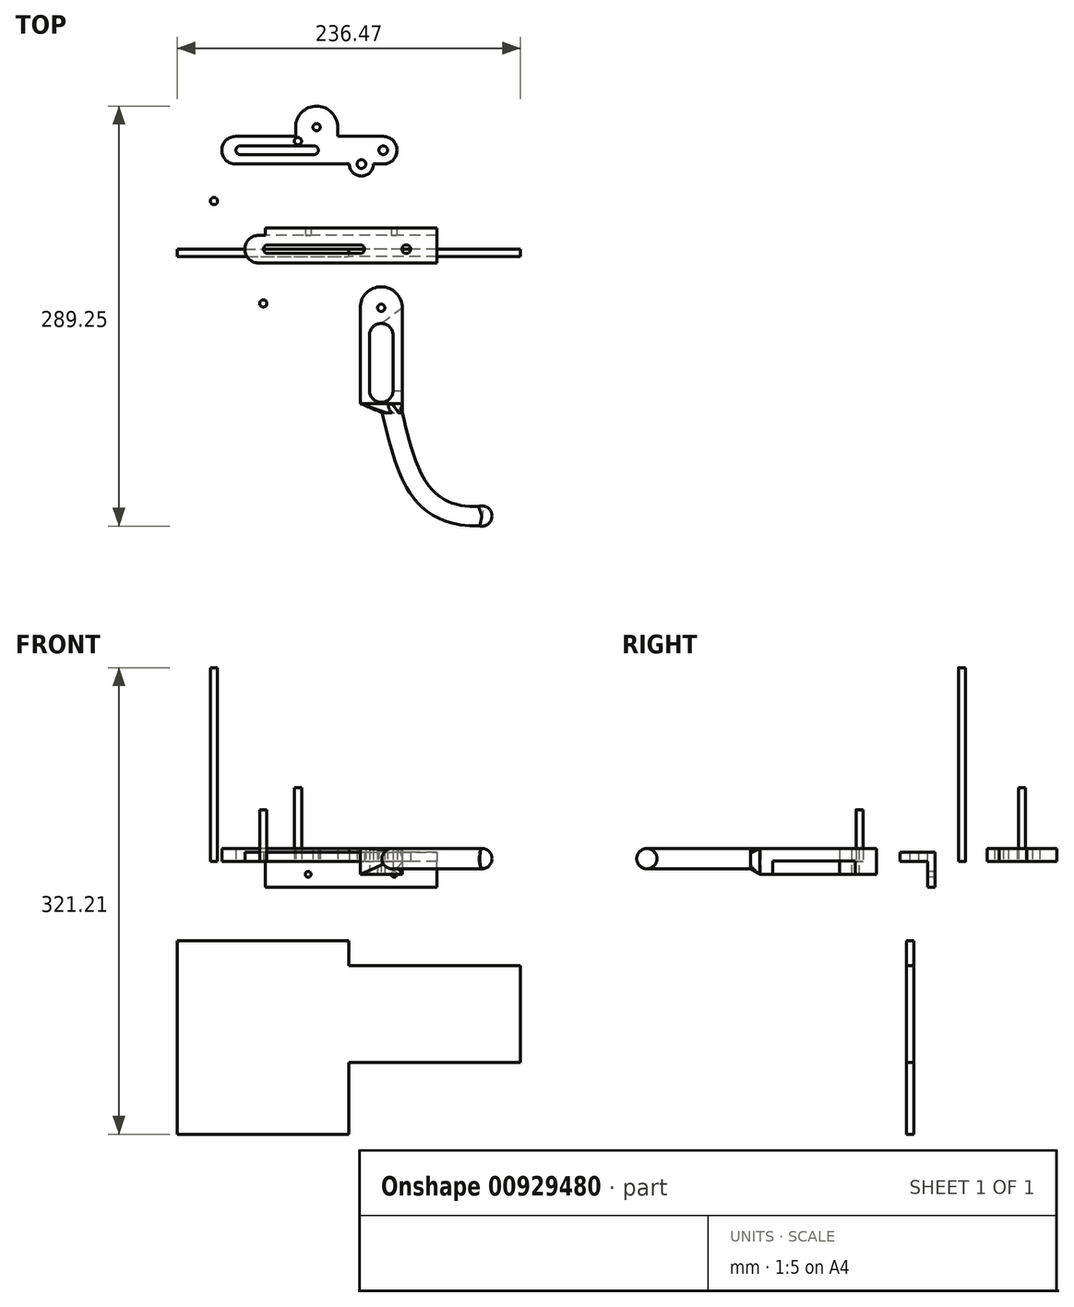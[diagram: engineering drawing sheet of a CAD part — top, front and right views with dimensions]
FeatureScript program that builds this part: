
annotation { "Feature Type Name" : "Feature", "Feature Type Description" : "" }
export const myFeature = defineFeature(function(context is Context, id is Id, definition is map)
    precondition{}
    {
        {
            var Q0;
            Q0=qCreatedBy(makeId("Top.planeOp"),FACE);
            var sketch = newSketch(context, id + "F0", { "sketchPlane" : qUnion([Q0])});
            skLineSegment(sketch, "E0.bottom", {"start": v(63.5, 9.53) * mm, "end": v(-38.1, 9.52) * mm});
            skLineSegment(sketch, "E0.top", {"start": v(63.5, -9.52) * mm, "end": v(-38.1, -9.53) * mm});
            skPoint(sketch, "E0.middle", {"position": v(0, 0) * mm});
            skLineSegment(sketch, "E1.bottom", {"start": v(31.75, 3) * mm, "end": v(-31.75, 3) * mm});
            skLineSegment(sketch, "E1.top", {"start": v(31.75, -3) * mm, "end": v(-31.75, -3) * mm});
            skArc(sketch, "E2", {"start": v(-31.75, 3) * mm, "mid": v(-34.75, 0) * mm, "end": v(-31.75, -3) * mm});
            skArc(sketch, "E3", {"start": v(31.75, -3) * mm, "mid": v(34.75, 0) * mm, "end": v(31.75, 3) * mm});
            skArc(sketch, "E4", {"start": v(-38.1, 9.52) * mm, "mid": v(-47.62, 0) * mm, "end": v(-38.1, -9.53) * mm});
            skLineSegment(sketch, "E5.bottom", {"start": v(63.5, 9.53) * mm, "end": v(84.7, 9.53) * mm});
            skLineSegment(sketch, "E5.top", {"start": v(63.5, -9.52) * mm, "end": v(84.7, -9.52) * mm});
            skLineSegment(sketch, "E5.right", {"start": v(84.7, 9.53) * mm, "end": v(84.7, -9.52) * mm});
            skCircle(sketch, "E6", {"center": v(63.5, 0) * mm, "radius": 3 * mm});
            skSolve(sketch);
        }
        {
            var Q0;
            Q0=makeQuery(id+"F0.imprint","IMPRINT",FACE,{"disambiguationData":[TD([[makeQuery(id+"F0.imprint","IMPRINT",EDGE,{"derivedFrom":sQuery(id+"F0.wireOp",EDGE,"E0.bottom")}),1.0]])]});
            extrude(context, id + "F1", {"entities" : qUnion([Q0]), "depth" : 6.35 * mm, "offsetDistance" : 25.4 * mm});
        }
        {
            var Q0;
            Q0=qCreatedBy(makeId("Top.planeOp"),FACE);
            var sketch = newSketch(context, id + "F2", { "sketchPlane" : qUnion([Q0])});
            skLineSegment(sketch, "E7.bottom", {"start": v(47.62, 77.65) * mm, "end": v(16.26, 77.65) * mm});
            skLineSegment(sketch, "E7.top", {"start": v(47.62, 58.6) * mm, "end": v(-53.98, 58.6) * mm});
            skLineSegment(sketch, "E8.bottom", {"start": v(0, 71.13) * mm, "end": v(-50.8, 71.13) * mm});
            skLineSegment(sketch, "E8.top", {"start": v(0, 65.13) * mm, "end": v(-50.8, 65.13) * mm});
            skPoint(sketch, "E8.middle", {"position": v(-25.4, 68.13) * mm});
            skArc(sketch, "E9", {"start": v(-50.8, 71.13) * mm, "mid": v(-53.8, 68.13) * mm, "end": v(-50.8, 65.13) * mm});
            skArc(sketch, "E10", {"start": v(0, 65.13) * mm, "mid": v(3, 68.13) * mm, "end": v(0, 71.13) * mm});
            skArc(sketch, "E11", {"start": v(-53.98, 77.65) * mm, "mid": v(-63.5, 68.13) * mm, "end": v(-53.98, 58.6) * mm});
            skArc(sketch, "E12", {"start": v(47.62, 58.6) * mm, "mid": v(57.15, 68.13) * mm, "end": v(47.62, 77.65) * mm});
            skLineSegment(sketch, "E13", {"start": v(-25.4, 77.65) * mm, "end": v(-25.4, 58.6) * mm, "construction": true});
            skCircle(sketch, "E14", {"center": v(47.62, 68.13) * mm, "radius": 3 * mm});
            skCircle(sketch, "E15", {"center": v(32.61, 58.6) * mm, "radius": 3 * mm});
            skArc(sketch, "E16", {"start": v(24.32, 58.6) * mm, "mid": v(32.61, 50.31) * mm, "end": v(40.9, 58.6) * mm});
            skArc(sketch, "E17", {"start": v(16.26, 84) * mm, "mid": v(1.78, 98.48) * mm, "end": v(-12.7, 84) * mm});
            skCircle(sketch, "E18", {"center": v(1.78, 84) * mm, "radius": 2.5 * mm});
            skLineSegment(sketch, "E19", {"start": v(-12.7, 77.65) * mm, "end": v(-12.7, 84) * mm});
            skLineSegment(sketch, "E20", {"start": v(16.26, 77.65) * mm, "end": v(16.26, 84) * mm});
            skLineSegment(sketch, "E21", {"start": v(-12.7, 77.65) * mm, "end": v(-53.98, 77.65) * mm});
            skSolve(sketch);
        }
        {
            var Q0;
            Q0=makeQuery(id+"F2.imprint","IMPRINT",FACE,{"disambiguationData":[TD([[makeQuery(id+"F2.imprint","IMPRINT",EDGE,{"derivedFrom":sQuery(id+"F2.wireOp",EDGE,"E7.bottom")}),1.0]])]});
            var Q1;
            {var subQ0=sQuery(id+"F2.wireOp",EDGE,"O4J8zJx1-k10I-jmTt-IUS2-t3sebLQ1dyLB");Q1=makeQuery(id+"F2.imprint","IMPRINT",FACE,{"disambiguationData":[TD([[makeQuery(id+"F2.imprint","IMPRINT",EDGE,{"derivedFrom":subQ0}),1.0]])]});}
            var Q2;
            {var subQ0=sQuery(id+"F2.wireOp",EDGE,"E16");Q2=makeQuery(id+"F2.imprint","IMPRINT",FACE,{"disambiguationData":[TD([[makeQuery(id+"F2.imprint","IMPRINT",EDGE,{"derivedFrom":subQ0}),1.0]])]});}
            extrude(context, id + "F3", {"entities" : qUnion([Q0, Q1, Q2]), "depth" : 9 * mm, "offsetDistance" : 25.4 * mm});
        }
        {
            var Q0;
            Q0=qCreatedBy(makeId("Top.planeOp"),FACE);
            var sketch = newSketch(context, id + "F4", { "sketchPlane" : qUnion([Q0])});
            skCircle(sketch, "E22", {"center": v(-11.08, 74.38) * mm, "radius": 2.5 * mm});
            skSolve(sketch);
        }
        {
            var Q0;
            Q0=makeQuery(id+"F4.imprint","IMPRINT",FACE,{"disambiguationData":[TD([[makeQuery(id+"F4.imprint","IMPRINT",EDGE,{"derivedFrom":sQuery(id+"F4.wireOp",EDGE,"E22")}),1.0]])]});
            extrude(context, id + "F5", {"entities" : qUnion([Q0]), "depth" : 50.8 * mm, "offsetDistance" : 25.4 * mm});
        }
        {
            var Q0;
            Q0=qCreatedBy(makeId("Top.planeOp"),FACE);
            var sketch = newSketch(context, id + "F6", { "sketchPlane" : qUnion([Q0])});
            skCircle(sketch, "E23", {"center": v(-34.92, -37.39) * mm, "radius": 2.5 * mm});
            skSolve(sketch);
        }
        {
            var Q0;
            Q0=makeQuery(id+"F6.imprint","IMPRINT",FACE,{"disambiguationData":[TD([[makeQuery(id+"F6.imprint","IMPRINT",EDGE,{"derivedFrom":sQuery(id+"F6.wireOp",EDGE,"E23")}),1.0]])]});
            extrude(context, id + "F7", {"entities" : qUnion([Q0]), "depth" : 35.56 * mm, "offsetDistance" : 25.4 * mm});
        }
        {
            var Q0;
            Q0=qCreatedBy(makeId("Top.planeOp"),FACE);
            var sketch = newSketch(context, id + "F8", { "sketchPlane" : qUnion([Q0])});
            skArc(sketch, "E24", {"start": v(54.38, -59.26) * mm, "mid": v(46.25, -51.13) * mm, "end": v(38.12, -59.26) * mm});
            skLineSegment(sketch, "E25.left", {"start": v(38.12, -59.26) * mm, "end": v(38.12, -97.36) * mm});
            skLineSegment(sketch, "E25.right", {"start": v(54.38, -59.26) * mm, "end": v(54.38, -97.36) * mm});
            skArc(sketch, "E26", {"start": v(38.12, -97.36) * mm, "mid": v(46.25, -105.49) * mm, "end": v(54.38, -97.36) * mm});
            skLineSegment(sketch, "E27.0", {"start": v(31.77, -62.87) * mm, "end": v(31.77, -97.36) * mm});
            skLineSegment(sketch, "E27.2", {"start": v(60.73, -62.87) * mm, "end": v(60.73, -97.36) * mm});
            skLineSegment(sketch, "E28.left", {"start": v(60.73, -62.87) * mm, "end": v(60.73, -40.39) * mm});
            skLineSegment(sketch, "E28.right", {"start": v(31.77, -62.87) * mm, "end": v(31.77, -40.39) * mm});
            skArc(sketch, "E29", {"start": v(60.73, -40.39) * mm, "mid": v(46.25, -25.91) * mm, "end": v(31.77, -40.39) * mm});
            skCircle(sketch, "E30", {"center": v(46.25, -40.39) * mm, "radius": 2.5 * mm});
            skLineSegment(sketch, "E31", {"start": v(60.73, -97.36) * mm, "end": v(60.73, -106.25) * mm});
            skLineSegment(sketch, "E32", {"start": v(60.73, -106.25) * mm, "end": v(31.77, -106.25) * mm});
            skLineSegment(sketch, "E33", {"start": v(31.77, -106.25) * mm, "end": v(31.77, -97.36) * mm});
            skSolve(sketch);
        }
        {
            var Q0;
            Q0=makeQuery(id+"F8.imprint","IMPRINT",FACE,{"disambiguationData":[TD([[makeQuery(id+"F8.imprint","IMPRINT",EDGE,{"derivedFrom":sQuery(id+"F8.wireOp",EDGE,"E24")}),-1.0]])]});
            extrude(context, id + "F9", {"entities" : qUnion([Q0]), "depth" : 8.9 * mm, "offsetDistance" : 25.4 * mm, "hasSecondDirection" : true, "secondDirectionOppositeDirection" : true, "secondDirectionDepth" : 8.9 * mm});
        }
        {
            var Q0;
            Q0=makeQuery(id+"F9.opExtrude","SWEPT_FACE",FACE,{"disambiguationData":[OSD([sQuery(id+"F8.wireOp",EDGE,"E32")])]});
            var sketch = newSketch(context, id + "F10", { "sketchPlane" : qUnion([Q0])});
            skLineSegment(sketch, "E34.bottom", {"start": v(31.77, 8.9) * mm, "end": v(60.73, 8.9) * mm});
            skLineSegment(sketch, "E34.top", {"start": v(31.77, -8.9) * mm, "end": v(60.73, -8.9) * mm});
            skLineSegment(sketch, "E34.left", {"start": v(31.77, 8.9) * mm, "end": v(31.77, -8.9) * mm});
            skLineSegment(sketch, "E34.right", {"start": v(60.73, 8.9) * mm, "end": v(60.73, -8.9) * mm});
            skSolve(sketch);
        }
        {
            var Q0;
            Q0=makeQuery(id+"F10.imprint","IMPRINT",FACE,{"disambiguationData":[TD([[makeQuery(id+"F10.imprint","IMPRINT",EDGE,{"derivedFrom":sQuery(id+"F10.wireOp",EDGE,"E34.bottom")}),1.0]])]});
            cPlane(context, id + "F11", {"entities" : qUnion([Q0]), "cplaneType" : CPlaneType.OFFSET, "offset" : 6.35 * mm, "width" : 152.4 * mm, "height" : 152.4 * mm});
        }
        {
            var Q0;
            Q0=qCreatedBy(id+"F11.planeOp",FACE);
            var sketch = newSketch(context, id + "F12", { "sketchPlane" : qUnion([Q0])});
            skCircle(sketch, "E35", {"center": v(53.74, 1.9) * mm, "radius": 6.99 * mm});
            skSolve(sketch);
        }
        {
            var Q0;
            Q0 = qConstructionFilter(qBodyType(qCreatedBy(id + "F14" ,EDGE), BodyType.WIRE), ConstructionObject.NO);
            var Q2;
            Q2 = qSketchRegion(id + "F12", true);
            var Q3;
            Q3 = qSketchRegion(id + "F10", true);
            loft(context, id + "F13", {"operationType" : NewBodyOperationType.ADD, "addSections" : true, "spine" : qUnion([Q0]), "sectionCount" : 5, "sheetProfilesArray" : [{ "sheetProfileEntities" : qUnion([Q2]) }, { "sheetProfileEntities" : qUnion([Q3]) }]});
        }
        {
            var Q0;
            Q0=qCreatedBy(makeId("Top.planeOp"),FACE);
            var sketch = newSketch(context, id + "F14", { "sketchPlane" : qUnion([Q0])});
            skFitSpline(sketch, "E36", {"points": [v(45.7, -106.78) * mm, v(65.36, -166.04) * mm, v(114.23, -190.13) * mm], "startDerivative": vector(26.63, -91.36) * mm, "endDerivative": vector(138.48, 6.35) * mm});
            skSolve(sketch);
        }
        {
            var Q0;
            Q0=makeQuery(id+"F13.opLoft","CAP_FACE",FACE,{"disambiguationData":[OSD([makeQuery(id+"F12.imprint","IMPRINT",FACE,{"disambiguationData":[TD([[makeQuery(id+"F12.imprint","IMPRINT",EDGE,{"derivedFrom":sQuery(id+"F12.wireOp",EDGE,"E35")}),1.0]])]})])],"isStart":true});
            var Q1;
            Q1=sQuery(id+"F14.wireOp",EDGE,"E36");
            sweep(context, id + "F15", {"operationType" : NewBodyOperationType.ADD, "profiles" : qUnion([Q0]), "path" : qUnion([Q1])});
        }
        {
            var Q0;
            Q0=makeQuery(id+"F9.opExtrude","CAP_FACE",FACE,{"disambiguationData":[OSD([sQuery(id+"F8.wireOp",EDGE,"E24"),sQuery(id+"F8.wireOp",EDGE,"E25.left"),sQuery(id+"F8.wireOp",EDGE,"E25.right"),sQuery(id+"F8.wireOp",EDGE,"E26"),sQuery(id+"F8.wireOp",EDGE,"E27.0"),sQuery(id+"F8.wireOp",EDGE,"E27.2"),sQuery(id+"F8.wireOp",EDGE,"E28.left"),sQuery(id+"F8.wireOp",EDGE,"E28.right"),sQuery(id+"F8.wireOp",EDGE,"E29"),sQuery(id+"F8.wireOp",EDGE,"E30"),sQuery(id+"F8.wireOp",EDGE,"E31"),sQuery(id+"F8.wireOp",EDGE,"E32"),sQuery(id+"F8.wireOp",EDGE,"E33")])],"isStart":true});
            var sketch = newSketch(context, id + "F16", { "sketchPlane" : qUnion([Q0])});
            skLineSegment(sketch, "E37.bottom", {"start": v(46.25, 97.36) * mm, "end": v(60.73, 97.36) * mm});
            skLineSegment(sketch, "E37.top", {"start": v(46.25, 51.13) * mm, "end": v(60.73, 40.39) * mm});
            skLineSegment(sketch, "E37.left", {"start": v(46.25, 97.36) * mm, "end": v(46.25, 51.13) * mm});
            skLineSegment(sketch, "E37.right", {"start": v(60.73, 97.36) * mm, "end": v(60.73, 40.39) * mm});
            skPoint(sketch, "E38", {"position": v(46.25, 51.13) * mm});
            skSolve(sketch);
        }
        {
            var Q0;
            {var subQ3=sQuery(id+"F16.wireOp",EDGE,"E37.bottom");Q0=makeQuery(id+"F16.imprint","IMPRINT",FACE,{"disambiguationData":[TD([[makeQuery(id+"F16.imprint","IMPRINT",EDGE,{"derivedFrom":subQ3}),-1.0]])]});}
            var Q1;
            {var subQ1=sQuery(id+"F16.wireOp",EDGE,"E37.top");Q1=makeQuery(id+"F16.imprint","IMPRINT",FACE,{"disambiguationData":[TD([[makeQuery(id+"F16.imprint","IMPRINT",EDGE,{"derivedFrom":subQ1}),1.0]])]});}
            extrude(context, id + "F17", {"entities" : qUnion([Q0, Q1]), "operationType" : NewBodyOperationType.REMOVE, "oppositeDirection" : true, "depth" : 9.14 * mm, "offsetDistance" : 25.4 * mm});
        }
        {
            var Q0;
            Q0=makeQuery(id+"F15.opSweep","CAP_FACE",FACE,{"disambiguationData":[OSD([makeQuery(id+"F12.imprint","IMPRINT",FACE,{"disambiguationData":[TD([[makeQuery(id+"F12.imprint","IMPRINT",EDGE,{"derivedFrom":sQuery(id+"F12.wireOp",EDGE,"E35")}),1.0]])]}),sQuery(id+"F14.wireOp",VERTEX,"E36.end")])],"isStart":false});
            var sketch = newSketch(context, id + "F18", { "sketchPlane" : qUnion([Q0])});
            skCircle(sketch, "E39", {"center": v(-156.48, 1.9) * mm, "radius": 6.99 * mm});
            skLineSegment(sketch, "E40", {"start": v(-162.34, -1.89) * mm, "end": v(-150.61, 5.7) * mm});
            skSolve(sketch);
        }
        {
            var Q0;
            {var subQ2=sQuery(id+"F18.wireOp",EDGE,"E40");Q0=makeQuery(id+"F18.imprint","IMPRINT",FACE,{"disambiguationData":[TD([[makeQuery(id+"F18.imprint","IMPRINT",EDGE,{"derivedFrom":subQ2}),1.0]])]});}
            var Q1;
            Q1=sQuery(id+"F18.wireOp",EDGE,"E40");
            revolve(context, id + "F19", {"operationType" : NewBodyOperationType.ADD, "surfaceOperationType" : NewSurfaceOperationType.NEW, "entities" : qUnion([Q0]), "axis" : qUnion([Q1]), "revolveType" : RevolveType.FULL});
        }
        {
            var Q0;
            Q0=qCreatedBy(makeId("Top.planeOp"),FACE);
            var sketch = newSketch(context, id + "F20", { "sketchPlane" : qUnion([Q0])});
            skCircle(sketch, "E41", {"center": v(-68.9, 33.13) * mm, "radius": 2.5 * mm});
            skSolve(sketch);
        }
        {
            var Q0;
            Q0=qCreatedBy(makeId("Top.planeOp"),FACE);
            var sketch = newSketch(context, id + "F21", { "sketchPlane" : qUnion([Q0])});
            skLineSegment(sketch, "E42.bottom", {"start": v(84.7, 14.6) * mm, "end": v(-33.62, 14.6) * mm});
            skLineSegment(sketch, "E42.top", {"start": v(84.7, 9.53) * mm, "end": v(-33.62, 9.52) * mm});
            skLineSegment(sketch, "E42.left", {"start": v(84.7, 9.53) * mm, "end": v(84.7, 14.6) * mm});
            skLineSegment(sketch, "E42.right", {"start": v(-33.62, 9.52) * mm, "end": v(-33.62, 14.6) * mm});
            skSolve(sketch);
        }
        {
            var Q0;
            Q0=makeQuery(id+"F21.imprint","IMPRINT",FACE,{"disambiguationData":[TD([[makeQuery(id+"F21.imprint","IMPRINT",EDGE,{"derivedFrom":sQuery(id+"F21.wireOp",EDGE,"E42.bottom")}),-1.0]])]});
            var Q1;
            Q1=makeQuery(id+"F21.imprint","IMPRINT",FACE,{"disambiguationData":[TD([[makeQuery(id+"F21.imprint","IMPRINT",EDGE,{"derivedFrom":sQuery(id+"F21.wireOp",EDGE,"E42.bottom")}),1.0]])]});
            var Q2;
            Q2=makeQuery(id+"F1.opExtrude","CAP_FACE",FACE,{"disambiguationData":[OSD([sQuery(id+"F0.wireOp",EDGE,"E0.bottom"),sQuery(id+"F0.wireOp",EDGE,"E0.top"),sQuery(id+"F0.wireOp",EDGE,"E1.bottom"),sQuery(id+"F0.wireOp",EDGE,"E1.top"),sQuery(id+"F0.wireOp",EDGE,"E2"),sQuery(id+"F0.wireOp",EDGE,"E3"),sQuery(id+"F0.wireOp",EDGE,"E4"),sQuery(id+"F0.wireOp",EDGE,"E5.bottom"),sQuery(id+"F0.wireOp",EDGE,"E5.top"),sQuery(id+"F0.wireOp",EDGE,"E5.right"),sQuery(id+"F0.wireOp",EDGE,"E6")])],"isStart":false});
            extrude(context, id + "F22", {"entities" : qUnion([Q0, Q1]), "operationType" : NewBodyOperationType.ADD, "oppositeDirection" : true, "depth" : 17.78 * mm, "offsetDistance" : 25.4 * mm, "hasSecondDirection" : true, "secondDirectionBound" : SecondDirectionBoundingType.UP_TO_SURFACE, "secondDirectionOppositeDirection" : false, "secondDirectionDepth" : 25.4 * mm, "secondDirectionBoundEntityFace" : qUnion([Q2])});
        }
        {
            var Q0;
            Q0 = qSketchRegion(id + "F20", true);
            extrude(context, id + "F23", {"entities" : qUnion([Q0]), "depth" : 133.35 * mm, "offsetDistance" : 25.4 * mm});
        }
        {
            var Q0;
            Q0=makeQuery(id+"F22.opExtrude","SWEPT_FACE",FACE,{"disambiguationData":[OSD([sQuery(id+"F21.wireOp",EDGE,"E42.top")])]});
            var sketch = newSketch(context, id + "F24", { "sketchPlane" : qUnion([Q0])});
            skCircle(sketch, "E43", {"center": v(55.13, -8.9) * mm, "radius": 2 * mm});
            skPoint(sketch, "E44", {"position": v(25.55, -8.9) * mm});
            skLineSegment(sketch, "E45", {"start": v(-33.62, -8.9) * mm, "end": v(-6.04, -8.9) * mm, "construction": true});
            skLineSegment(sketch, "E46", {"start": v(84.7, -8.89) * mm, "end": v(57.13, -8.9) * mm, "construction": true});
            skCircle(sketch, "E47", {"center": v(-4.04, -8.9) * mm, "radius": 2 * mm});
            skLineSegment(sketch, "E48.trimOffspring", {"start": v(-2.04, -8.9) * mm, "end": v(25.55, -8.9) * mm, "construction": true});
            skLineSegment(sketch, "E49.trimOffspring", {"start": v(53.13, -8.9) * mm, "end": v(25.55, -8.9) * mm, "construction": true});
            skSolve(sketch);
        }
        {
            var Q0;
            Q0=makeQuery(id+"F24.imprint","IMPRINT",FACE,{"disambiguationData":[TD([[makeQuery(id+"F24.imprint","IMPRINT",EDGE,{"derivedFrom":sQuery(id+"F24.wireOp",EDGE,"E47")}),1.0]])]});
            var Q1;
            Q1=makeQuery(id+"F24.imprint","IMPRINT",FACE,{"disambiguationData":[TD([[makeQuery(id+"F24.imprint","IMPRINT",EDGE,{"derivedFrom":sQuery(id+"F24.wireOp",EDGE,"E43")}),1.0]])]});
            extrude(context, id + "F25", {"entities" : qUnion([Q0, Q1]), "operationType" : NewBodyOperationType.REMOVE, "endBound" : BoundingType.THROUGH_ALL, "oppositeDirection" : true, "depth" : 25.4 * mm, "offsetDistance" : 25.4 * mm});
        }
        {
            var Q0;
            Q0=qCreatedBy(makeId("Front.planeOp"),FACE);
            var sketch = newSketch(context, id + "F26", { "sketchPlane" : qUnion([Q0])});
            skLineSegment(sketch, "E50.bottom", {"start": v(-94.3, -187.86) * mm, "end": v(24.06, -187.86) * mm});
            skLineSegment(sketch, "E50.top", {"start": v(-94.3, -54.76) * mm, "end": v(24.06, -54.76) * mm});
            skLineSegment(sketch, "E50.left", {"start": v(-94.3, -187.86) * mm, "end": v(-94.3, -54.76) * mm});
            skLineSegment(sketch, "E50.right", {"start": v(142.17, -138.3) * mm, "end": v(142.17, -71.75) * mm});
            skLineSegment(sketch, "E51.bottom", {"start": v(142.17, -71.75) * mm, "end": v(24.06, -71.75) * mm});
            skLineSegment(sketch, "E51.top", {"start": v(142.17, -138.3) * mm, "end": v(24.06, -138.3) * mm});
            skLineSegment(sketch, "E51.left", {"start": v(142.17, -71.75) * mm, "end": v(142.17, -138.3) * mm});
            skLineSegment(sketch, "E52", {"start": v(24.06, -71.75) * mm, "end": v(24.06, -54.76) * mm});
            skLineSegment(sketch, "E53", {"start": v(24.06, -138.3) * mm, "end": v(24.06, -187.86) * mm});
            skSolve(sketch);
        }
        {
            var Q0;
            Q0=makeQuery(id+"F26.imprint","IMPRINT",FACE,{"disambiguationData":[TD([[makeQuery(id+"F26.imprint","IMPRINT",EDGE,{"derivedFrom":sQuery(id+"F26.wireOp",EDGE,"E50.bottom")}),1.0]])]});
            extrude(context, id + "F27", {"entities" : qUnion([Q0]), "depth" : 5.08 * mm, "offsetDistance" : 25.4 * mm});
        }
    });
